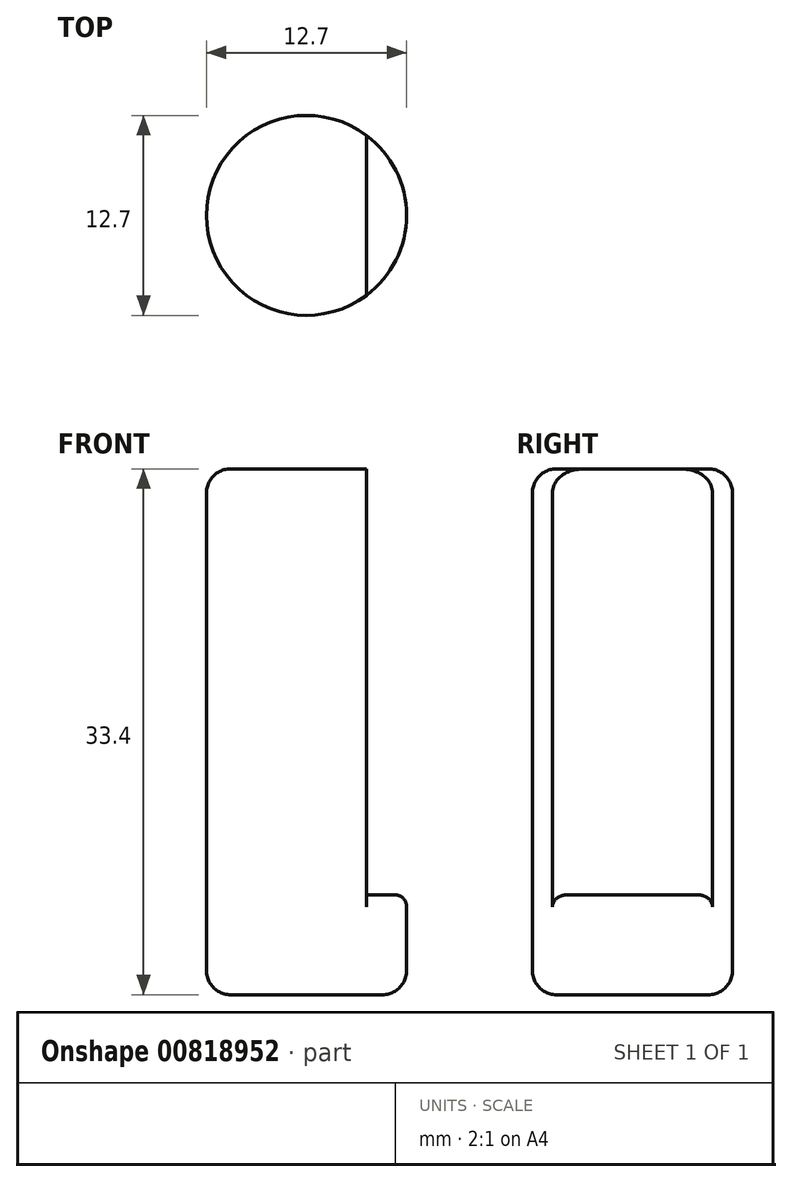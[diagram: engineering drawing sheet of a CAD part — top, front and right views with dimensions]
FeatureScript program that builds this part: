
annotation { "Feature Type Name" : "Feature", "Feature Type Description" : "" }
export const myFeature = defineFeature(function(context is Context, id is Id, definition is map)
    precondition{}
    {
        {
            var Q0;
            Q0=qCreatedBy(makeId("Front.planeOp"),FACE);
            var sketch = newSketch(context, id + "F0", { "sketchPlane" : qUnion([Q0])});
            skLineSegment(sketch, "E0", {"start": v(0, 0) * mm, "end": v(0, 33.4) * mm});
            skLineSegment(sketch, "E1", {"start": v(0, 33.4) * mm, "end": v(6.35, 33.4) * mm});
            skLineSegment(sketch, "E2", {"start": v(6.35, 33.4) * mm, "end": v(6.35, 0) * mm});
            skLineSegment(sketch, "E3", {"start": v(6.35, 0) * mm, "end": v(0, 0) * mm});
            skSolve(sketch);
        }
        {
            var Q0;
            Q0 = qSketchRegion(id + "F0", true);
            var Q1;
            Q1=sQuery(id+"F0.wireOp",EDGE,"E0");
            revolve(context, id + "F1", {"surfaceOperationType" : NewSurfaceOperationType.NEW, "entities" : qUnion([Q0]), "axis" : qUnion([Q1]), "revolveType" : RevolveType.FULL});
        }
        {
            var Q0;
            Q0=makeQuery(id+"F1.opRevolve","SWEPT_FACE",FACE,{"disambiguationData":[OSD([sQuery(id+"F0.wireOp",EDGE,"E2")])]});
            fillet(context, id + "F2", {"entities" : qUnion([Q0]), "radius" : 1.52 * mm, "tangentPropagation" : true, "allowEdgeOverflow" : false});
        }
        {
            var Q0;
            Q0=qCreatedBy(makeId("Front.planeOp"),FACE);
            var sketch = newSketch(context, id + "F3", { "sketchPlane" : qUnion([Q0])});
            skLineSegment(sketch, "E4", {"start": v(8.9, 6.35) * mm, "end": v(3.8, 6.35) * mm});
            skLineSegment(sketch, "E5", {"start": v(3.81, 6.35) * mm, "end": v(3.81, 34.57) * mm});
            skLineSegment(sketch, "E6", {"start": v(3.81, 34.57) * mm, "end": v(8.9, 34.57) * mm});
            skLineSegment(sketch, "E7", {"start": v(8.9, 34.57) * mm, "end": v(8.9, 6.35) * mm});
            skLineSegment(sketch, "E8", {"start": v(0, 0) * mm, "end": v(6.35, 0) * mm, "construction": true});
            skPoint(sketch, "E8.endSnap0", {"position": v(6.35, 6.35) * mm});
            skSolve(sketch);
        }
        {
            var Q0;
            Q0 = qSketchRegion(id + "F3", true);
            extrude(context, id + "F4", {"entities" : qUnion([Q0]), "operationType" : NewBodyOperationType.REMOVE, "endBound" : BoundingType.SYMMETRIC, "oppositeDirection" : true, "depth" : 25.4 * mm, "offsetDistance" : 25.4 * mm});
        }
        {
            var Q0;
            Q0=makeQuery(id+"F4.boolean.opBoolean","INTERSECT",EDGE,{"derivedFrom":[makeQuery(id+"F1.opRevolve","SWEPT_FACE",FACE,{"disambiguationData":[OSD([sQuery(id+"F0.wireOp",EDGE,"E2")])]}),makeQuery(id+"F4.opExtrude","SWEPT_FACE",FACE,{"disambiguationData":[OSD([sQuery(id+"F3.wireOp",EDGE,"E4")])]})]});
            fillet(context, id + "F5", {"entities" : qUnion([Q0]), "radius" : 0.76 * mm, "tangentPropagation" : true, "allowEdgeOverflow" : false});
        }
    });
